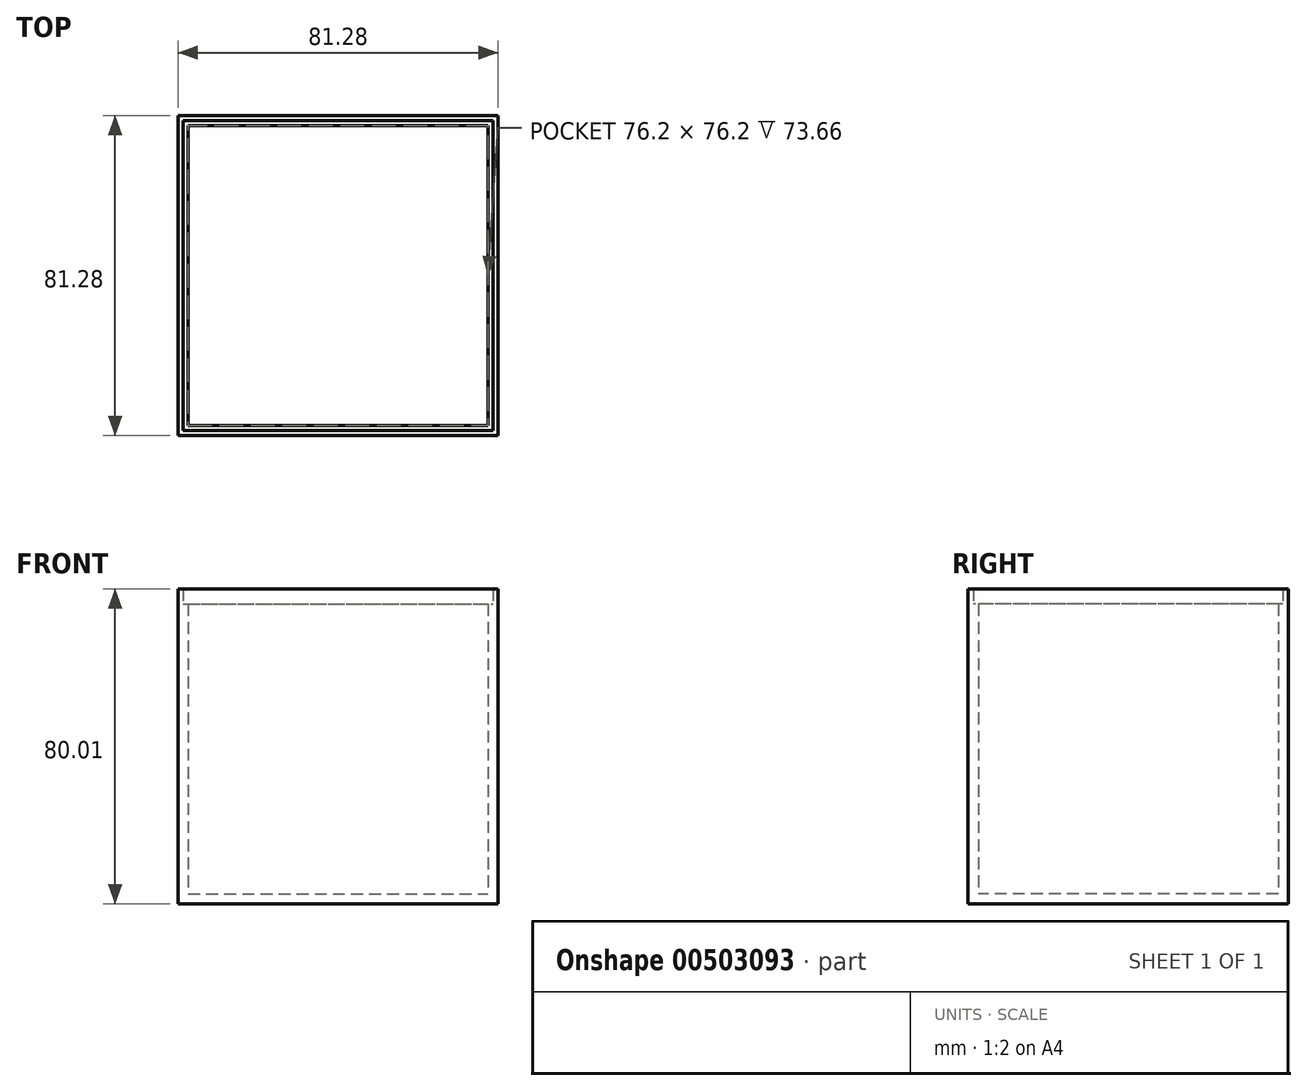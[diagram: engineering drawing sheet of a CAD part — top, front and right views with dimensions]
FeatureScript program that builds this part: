
annotation { "Feature Type Name" : "Feature", "Feature Type Description" : "" }
export const myFeature = defineFeature(function(context is Context, id is Id, definition is map)
    precondition{}
    {
        {
            var Q0;
            Q0=qCreatedBy(makeId("Top.planeOp"),FACE);
            var sketch = newSketch(context, id + "F0", { "sketchPlane" : qUnion([Q0])});
            skLineSegment(sketch, "E0.bottom", {"start": v(-51.93, 35.71) * mm, "end": v(29.35, 35.71) * mm});
            skLineSegment(sketch, "E0.top", {"start": v(-51.93, -45.57) * mm, "end": v(29.35, -45.57) * mm});
            skLineSegment(sketch, "E0.left", {"start": v(-51.93, 35.71) * mm, "end": v(-51.93, -45.57) * mm});
            skLineSegment(sketch, "E0.right", {"start": v(29.35, 35.71) * mm, "end": v(29.35, -45.57) * mm});
            skLineSegment(sketch, "E1.bottom", {"start": v(-49.39, 33.17) * mm, "end": v(26.81, 33.17) * mm});
            skLineSegment(sketch, "E1.top", {"start": v(-49.39, -43.03) * mm, "end": v(26.81, -43.03) * mm});
            skLineSegment(sketch, "E1.left", {"start": v(-49.39, 33.17) * mm, "end": v(-49.39, -43.03) * mm});
            skLineSegment(sketch, "E1.right", {"start": v(26.81, 33.17) * mm, "end": v(26.81, -43.03) * mm});
            skLineSegment(sketch, "E2.bottom", {"start": v(-50.66, 34.44) * mm, "end": v(28.08, 34.44) * mm});
            skLineSegment(sketch, "E2.top", {"start": v(-50.66, -44.3) * mm, "end": v(28.08, -44.3) * mm});
            skLineSegment(sketch, "E2.left", {"start": v(-50.66, 34.44) * mm, "end": v(-50.66, -44.3) * mm});
            skLineSegment(sketch, "E2.right", {"start": v(28.08, 34.44) * mm, "end": v(28.08, -44.3) * mm});
            skSolve(sketch);
        }
        {
            var Q0;
            Q0=makeQuery(id+"F0.imprint","IMPRINT",FACE,{"disambiguationData":[TD([[makeQuery(id+"F0.imprint","IMPRINT",EDGE,{"derivedFrom":sQuery(id+"F0.wireOp",EDGE,"E1.bottom")}),-1.0]])]});
            extrude(context, id + "F1", {"entities" : qUnion([Q0]), "depth" : 2.54 * mm});
        }
        {
            var Q0;
            Q0=makeQuery(id+"F0.imprint","IMPRINT",FACE,{"disambiguationData":[TD([[makeQuery(id+"F0.imprint","IMPRINT",EDGE,{"derivedFrom":sQuery(id+"F0.wireOp",EDGE,"E1.bottom")}),1.0]])]});
            extrude(context, id + "F2", {"entities" : qUnion([Q0]), "operationType" : NewBodyOperationType.ADD, "depth" : 76.2 * mm});
        }
        {
            var Q0;
            Q0=makeQuery(id+"F0.imprint","IMPRINT",FACE,{"disambiguationData":[TD([[makeQuery(id+"F0.imprint","IMPRINT",EDGE,{"derivedFrom":sQuery(id+"F0.wireOp",EDGE,"E0.bottom")}),-1.0]])]});
            extrude(context, id + "F3", {"entities" : qUnion([Q0]), "operationType" : NewBodyOperationType.ADD, "depth" : 80 * mm});
        }
    });
